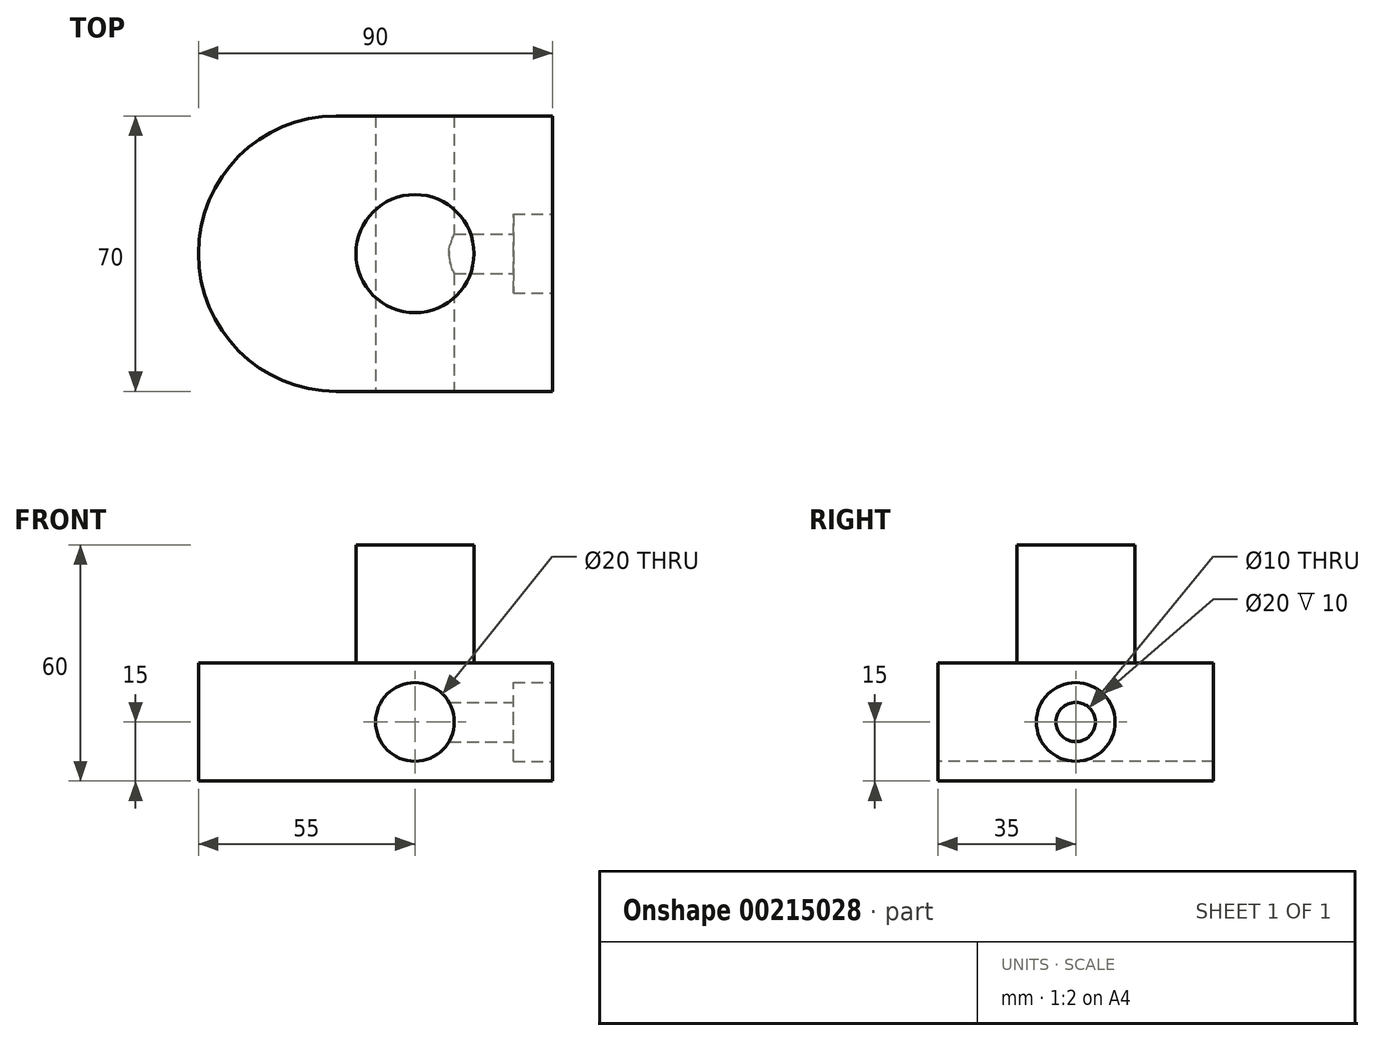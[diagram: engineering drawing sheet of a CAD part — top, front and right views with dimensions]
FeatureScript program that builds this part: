
annotation { "Feature Type Name" : "Feature", "Feature Type Description" : "" }
export const myFeature = defineFeature(function(context is Context, id is Id, definition is map)
    precondition{}
    {
        {
            var Q0;
            Q0=qCreatedBy(makeId("Top.planeOp"),FACE);
            var sketch = newSketch(context, id + "F0", { "sketchPlane" : qUnion([Q0])});
            skLineSegment(sketch, "E0.bottom", {"start": v(-45, 35) * mm, "end": v(45, 35) * mm});
            skLineSegment(sketch, "E0.top", {"start": v(-45, -35) * mm, "end": v(45, -35) * mm});
            skLineSegment(sketch, "E0.left", {"start": v(-45, 35) * mm, "end": v(-45, -35) * mm});
            skLineSegment(sketch, "E0.right", {"start": v(45, 35) * mm, "end": v(45, -35) * mm});
            skPoint(sketch, "E0.middle", {"position": v(0, 0) * mm});
            skSolve(sketch);
        }
        {
            var Q0;
            Q0=makeQuery(id+"F0.imprint","IMPRINT",FACE,{"disambiguationData":[TD([[makeQuery(id+"F0.imprint","IMPRINT",EDGE,{"derivedFrom":sQuery(id+"F0.wireOp",EDGE,"E0.bottom")}),-1.0]])]});
            extrude(context, id + "F1", {"entities" : qUnion([Q0]), "depth" : 30 * mm});
        }
        {
            var Q0;
            Q0=makeQuery(id+"F1.opExtrude","SWEPT_EDGE",EDGE,{"disambiguationData":[OSD([sQuery(id+"F0.wireOp",EDGE,"E0.bottom"),sQuery(id+"F0.wireOp",EDGE,"E0.left")])]});
            var Q1;
            Q1=makeQuery(id+"F1.opExtrude","SWEPT_EDGE",EDGE,{"disambiguationData":[OSD([sQuery(id+"F0.wireOp",EDGE,"E0.top"),sQuery(id+"F0.wireOp",EDGE,"E0.left")])]});
            fillet(context, id + "F2", {"entities" : qUnion([Q0, Q1]), "radius" : 35 * mm, "tangentPropagation" : true, "allowEdgeOverflow" : false});
        }
        {
            var Q0;
            Q0=makeQuery(id+"F1.opExtrude","SWEPT_FACE",FACE,{"disambiguationData":[OSD([sQuery(id+"F0.wireOp",EDGE,"E0.top")])]});
            var sketch = newSketch(context, id + "F3", { "sketchPlane" : qUnion([Q0])});
            skCircle(sketch, "E1", {"center": v(10, 15) * mm, "radius": 10 * mm});
            skSolve(sketch);
        }
        {
            var Q0;
            Q0=makeQuery(id+"F3.imprint","IMPRINT",FACE,{"disambiguationData":[TD([[makeQuery(id+"F3.imprint","IMPRINT",EDGE,{"derivedFrom":sQuery(id+"F3.wireOp",EDGE,"E1")}),1.0]])]});
            extrude(context, id + "F4", {"entities" : qUnion([Q0]), "operationType" : NewBodyOperationType.REMOVE, "endBound" : BoundingType.THROUGH_ALL, "oppositeDirection" : true, "depth" : 25 * mm});
        }
        {
            var Q0;
            Q0=makeQuery(id+"F1.opExtrude","SWEPT_FACE",FACE,{"disambiguationData":[OSD([sQuery(id+"F0.wireOp",EDGE,"E0.right")])]});
            var sketch = newSketch(context, id + "F5", { "sketchPlane" : qUnion([Q0])});
            skCircle(sketch, "E2", {"center": v(0, 15) * mm, "radius": 3.94 * mm});
            skPoint(sketch, "E2.centerSnap0", {"position": v(35, 15) * mm});
            skSolve(sketch);
        }
        {
            var Q0;
            Q0=sQuery(id+"F5.wireOp",VERTEX,"E2.center");
            var Q1;
            Q1=makeQuery(id+"F1.opExtrude","SWEPT_BODY",BODY,{"disambiguationData":[OSD([sQuery(id+"F0.wireOp",EDGE,"E0.bottom"),sQuery(id+"F0.wireOp",EDGE,"E0.top"),sQuery(id+"F0.wireOp",EDGE,"E0.left"),sQuery(id+"F0.wireOp",EDGE,"E0.right")])]});
            hole(context, id + "F6", {"style" : HoleStyle.C_BORE, "endStyle" : HoleEndStyle.BLIND, "holeDiameter" : 10 * mm, "cBoreDiameter" : 20 * mm, "cBoreDepth" : 10 * mm, "holeDepth" : 35 * mm, "locations" : qUnion([Q0]), "scope" : qUnion([Q1])});
        }
        {
            var Q0;
            Q0=makeQuery(id+"F1.opExtrude","CAP_FACE",FACE,{"disambiguationData":[OSD([sQuery(id+"F0.wireOp",EDGE,"E0.bottom"),sQuery(id+"F0.wireOp",EDGE,"E0.top"),sQuery(id+"F0.wireOp",EDGE,"E0.left"),sQuery(id+"F0.wireOp",EDGE,"E0.right")])],"isStart":false});
            var sketch = newSketch(context, id + "F7", { "sketchPlane" : qUnion([Q0])});
            skLineSegment(sketch, "E3", {"start": v(45, 0) * mm, "end": v(10, 0) * mm});
            skPoint(sketch, "E3.endSnap0", {"position": v(45, 0) * mm});
            skCircle(sketch, "E4", {"center": v(10, 0) * mm, "radius": 15 * mm});
            skSolve(sketch);
        }
        {
            var Q0;
            Q0=makeQuery(id+"F7.imprint","IMPRINT",FACE,{"disambiguationData":[TD([[makeQuery(id+"F7.imprint","IMPRINT",EDGE,{"derivedFrom":sQuery(id+"F7.wireOp",EDGE,"E4")}),1.0]])]});
            extrude(context, id + "F8", {"entities" : qUnion([Q0]), "operationType" : NewBodyOperationType.ADD, "depth" : 30 * mm});
        }
    });
